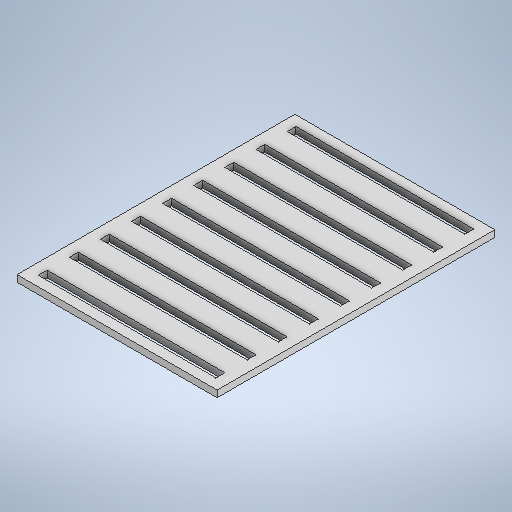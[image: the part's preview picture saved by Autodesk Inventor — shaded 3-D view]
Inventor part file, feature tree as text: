
AUTODESK INVENTOR PART (.ipt)
format: ipt  version: 2025 (Build 290162000, 162)  size: 305,664 bytes
history: native  units: in
note: dims shown in document units (in); Inventor stores cm internally (conversion verified against a paired STEP export)
features: extrude x1, sketch x1
ambient origin geometry x8: Origin, YZ Plane, XZ Plane, XY Plane, X Axis, Y Axis, Z Axis, Center Point
bodies: Solid1 (feature_tree)
feature tree (2):
  extrude  "Extrusion1"  Depth=35.4331in
  sketch  "Sketch1"  dims[d0=49.2126in d1=35.4331in d2=31.4961in d3=1.5748in d7=1.5748in d9=1.5748in d10=1.7717in d11=3.937in d12=3.937in d14=1.5748in d16=1.5748in d18=1.5748in d20=1.5748in d22=1.5748in d24=1.5748in d27=3.937in d28=3.937in d29=3.937in d30=3.937in d31=3.937in d32=3.937in d33=1.1811in d34=0.0in d36=1.9685in d37=0.1969in d38=0.0344in d39=0.1969in d40=0.0344in]
